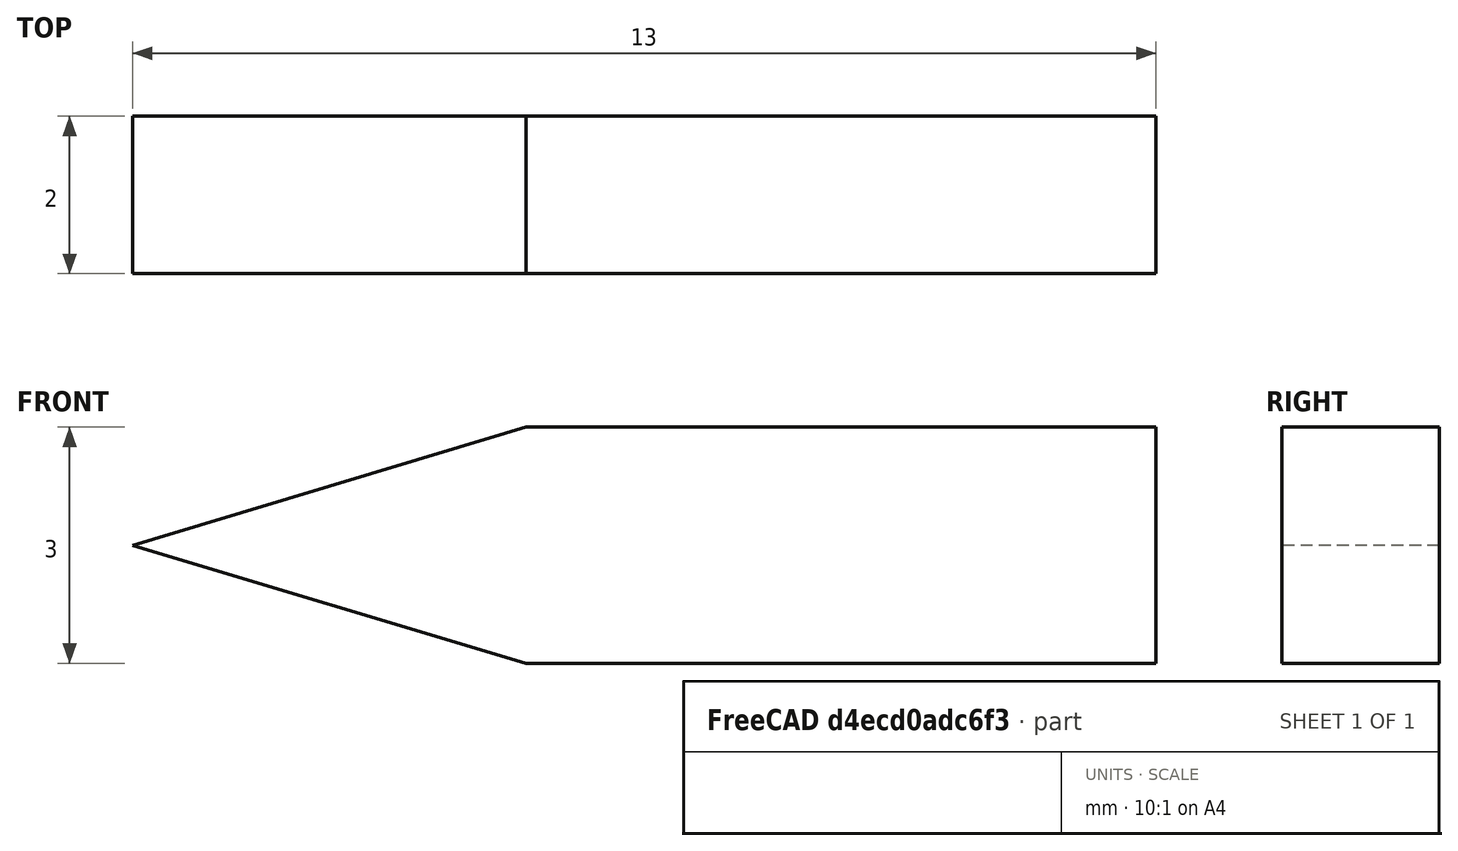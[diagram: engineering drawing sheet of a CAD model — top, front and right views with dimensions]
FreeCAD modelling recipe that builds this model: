
FCSTD DOCUMENT  (FreeCAD 0.18.4R)
Label: indicator2
License: All rights reserved
LicenseURL: http://en.wikipedia.org/wiki/All_rights_reserved
objects: Sketcher::SketchObject×1, PartDesign::Pad×1, PartDesign::Body×1
note: 4 computed .brp shape members not serialized (recipe doc carries the construction recipe); baked Part::Feature solids carry a one-line shape summary decoded from their .brp

FEATURE [Sketcher::SketchObject] Sketch
  MapMode = 5
  Placement = pos=(0,0,0) rot=(1,0,0;1.5708rad)
  Support = -> [XZ_Plane]
  sketch-geometry (5):
    g0: LineSegment StartX=0 StartY=1.5 StartZ=0 EndX=8 EndY=1.5 EndZ=0
    g1: LineSegment StartX=8 StartY=1.5 StartZ=0 EndX=8 EndY=-1.5 EndZ=0
    g2: LineSegment StartX=8 StartY=-1.5 StartZ=0 EndX=0 EndY=-1.5 EndZ=0
    g3: LineSegment StartX=0 StartY=1.5 StartZ=0 EndX=-5 EndY=0 EndZ=0
    g4: LineSegment StartX=-5 StartY=0 StartZ=0 EndX=0 EndY=-1.5 EndZ=0
  constraints (15):
    c: Coincident(g0,g1)
    c: Coincident(g1,g2)
    c: Horizontal(g0)
    c: Horizontal(g2)
    c: Vertical(g1)
    c: PointOnObject(g0,g-2)
    c: Coincident(g0,g3)
    c: PointOnObject(g3,g-1)
    c: Coincident(g3,g4)
    c: Coincident(g4,g2)
    c: DistanceY(g1,g1) = 3
    c: DistanceX(g0,g0) = 8
    c: DistanceX(g3,g0) = 5
    c: DistanceY(g-1,g0) = 1.5
    c: PointOnObject(g2,g-2)
FEATURE [PartDesign::Pad] Pad
  Length = 2
  Length2 = 100
  Placement = pos=(0,0,0) rot=(1,0,0;1.5708rad)
  Profile = -> Sketch
  Type = 0
FEATURE [PartDesign::Body] Body
  Group = -> [Sketch,Pad]
  Origin = -> Origin
  Tip = -> Pad
